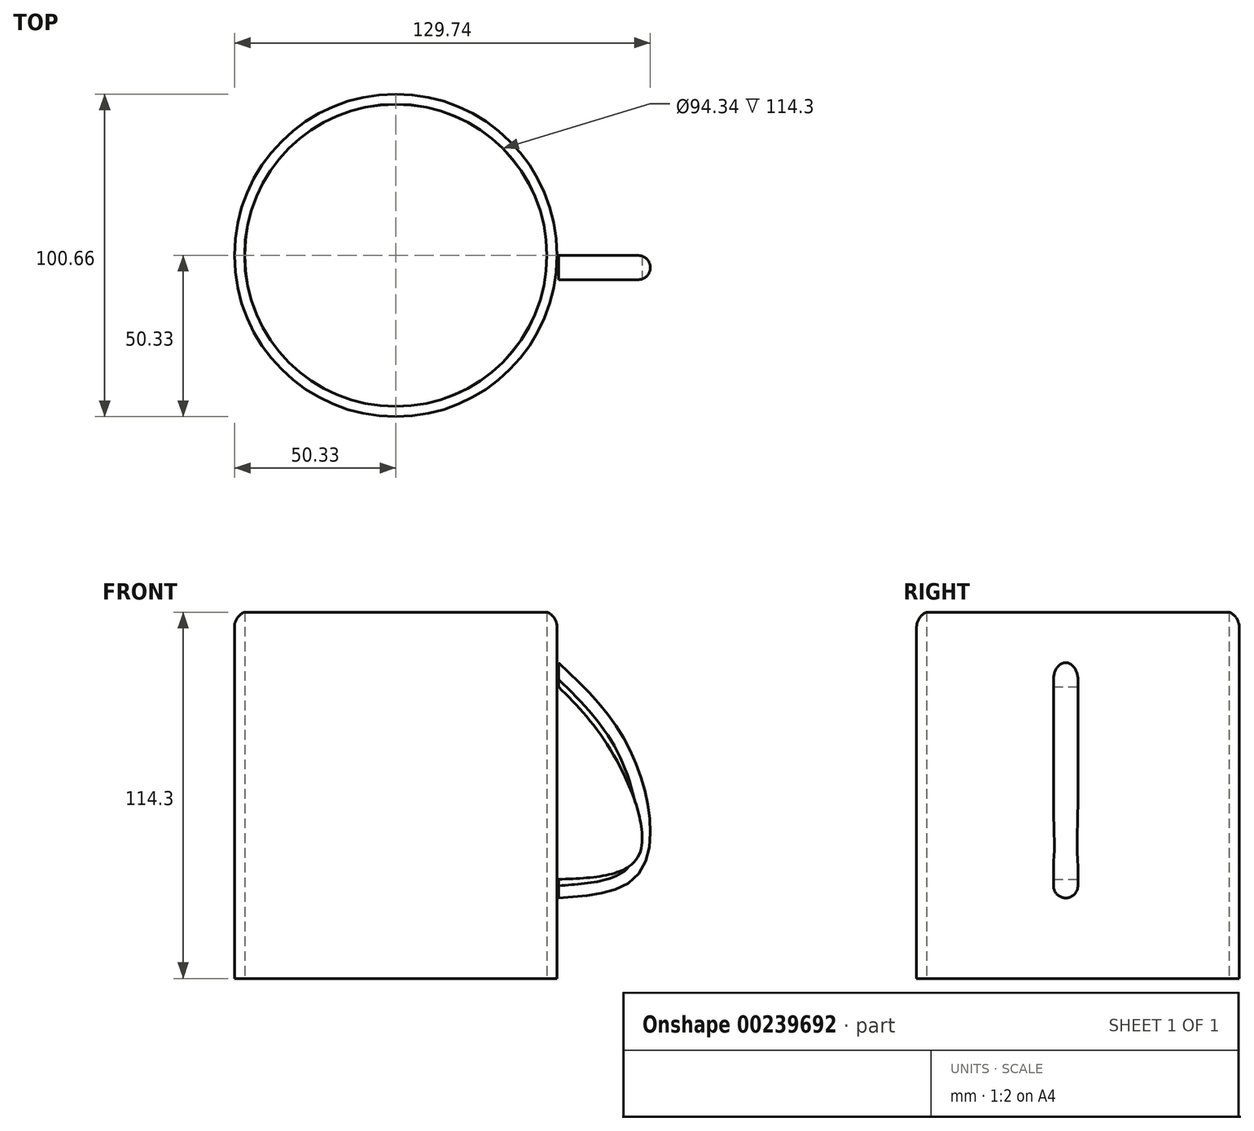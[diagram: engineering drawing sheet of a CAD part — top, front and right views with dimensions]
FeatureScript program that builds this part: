
annotation { "Feature Type Name" : "Feature", "Feature Type Description" : "" }
export const myFeature = defineFeature(function(context is Context, id is Id, definition is map)
    precondition{}
    {
        {
            var Q0;
            Q0=qCreatedBy(makeId("Top.planeOp"),FACE);
            var sketch = newSketch(context, id + "F0", { "sketchPlane" : qUnion([Q0])});
            skCircle(sketch, "E0", {"center": v(0, 0) * mm, "radius": 50.33 * mm});
            skCircle(sketch, "E1", {"center": v(0, 0) * mm, "radius": 47.16 * mm});
            skCircle(sketch, "E2", {"center": v(0, 0) * mm, "radius": 47.17 * mm});
            skSolve(sketch);
        }
        {
            var Q0;
            Q0=makeQuery(id+"F0.imprint","IMPRINT",FACE,{"disambiguationData":[TD([[makeQuery(id+"F0.imprint","IMPRINT",EDGE,{"derivedFrom":sQuery(id+"F0.wireOp",EDGE,"E0")}),1.0]])]});
            extrude(context, id + "F1", {"entities" : qUnion([Q0]), "depth" : 114.3 * mm});
        }
        {
            var Q0;
            Q0=makeQuery(id+"F0.imprint","IMPRINT",FACE,{"disambiguationData":[TD([[makeQuery(id+"F0.imprint","IMPRINT",EDGE,{"derivedFrom":sQuery(id+"F0.wireOp",EDGE,"E1")}),1.0]])]});
            extrude(context, id + "F2", {"entities" : qUnion([Q0]), "depth" : 0.03 * mm});
        }
        {
            var Q0;
            Q0=makeQuery(id+"F1.opExtrude","CAP_EDGE",EDGE,{"disambiguationData":[OSD([sQuery(id+"F0.wireOp",EDGE,"E0")])],"isStart":false});
            fillet(context, id + "F3", {"entities" : qUnion([Q0]), "radius" : 5.08 * mm, "tangentPropagation" : true, "allowEdgeOverflow" : false});
        }
        {
            var Q0;
            Q0=qCreatedBy(makeId("Front.planeOp"),FACE);
            var sketch = newSketch(context, id + "F4", { "sketchPlane" : qUnion([Q0])});
            skFitSpline(sketch, "E3", {"points": [v(50.78, 98.52) * mm, v(73.78, 69.83) * mm, v(76.37, 33.4) * mm, v(50.78, 25.12) * mm], "startDerivative": vector(74.52, -70.24) * mm, "endDerivative": vector(-104.68, -7.21) * mm});
            skFitSpline(sketch, "E4", {"points": [v(50.75, 91.04) * mm, v(67.93, 69.84) * mm, v(75.6, 38.04) * mm, v(50.75, 30.92) * mm], "startDerivative": vector(53.93, -54.35) * mm, "endDerivative": vector(-101.52, -4.03) * mm});
            skLineSegment(sketch, "E5", {"start": v(50.78, 98.52) * mm, "end": v(50.75, 91.04) * mm});
            skLineSegment(sketch, "E6", {"start": v(50.75, 30.92) * mm, "end": v(50.78, 25.12) * mm});
            skSolve(sketch);
        }
        {
            var Q0;
            Q0 = qSketchRegion(id + "F4", true);
            extrude(context, id + "F5", {"entities" : qUnion([Q0]), "depth" : 7.62 * mm});
        }
        {
            var Q0;
            Q0=makeQuery(id+"F5.opExtrude","CAP_EDGE",EDGE,{"disambiguationData":[OSD([sQuery(id+"F4.wireOp",EDGE,"E3")])],"isStart":true});
            var Q1;
            Q1=makeQuery(id+"F5.opExtrude","CAP_EDGE",EDGE,{"disambiguationData":[OSD([sQuery(id+"F4.wireOp",EDGE,"E3")])],"isStart":false});
            fillet(context, id + "F6", {"entities" : qUnion([Q0, Q1]), "radius" : 3.8 * mm, "tangentPropagation" : true, "allowEdgeOverflow" : false});
        }
    });
